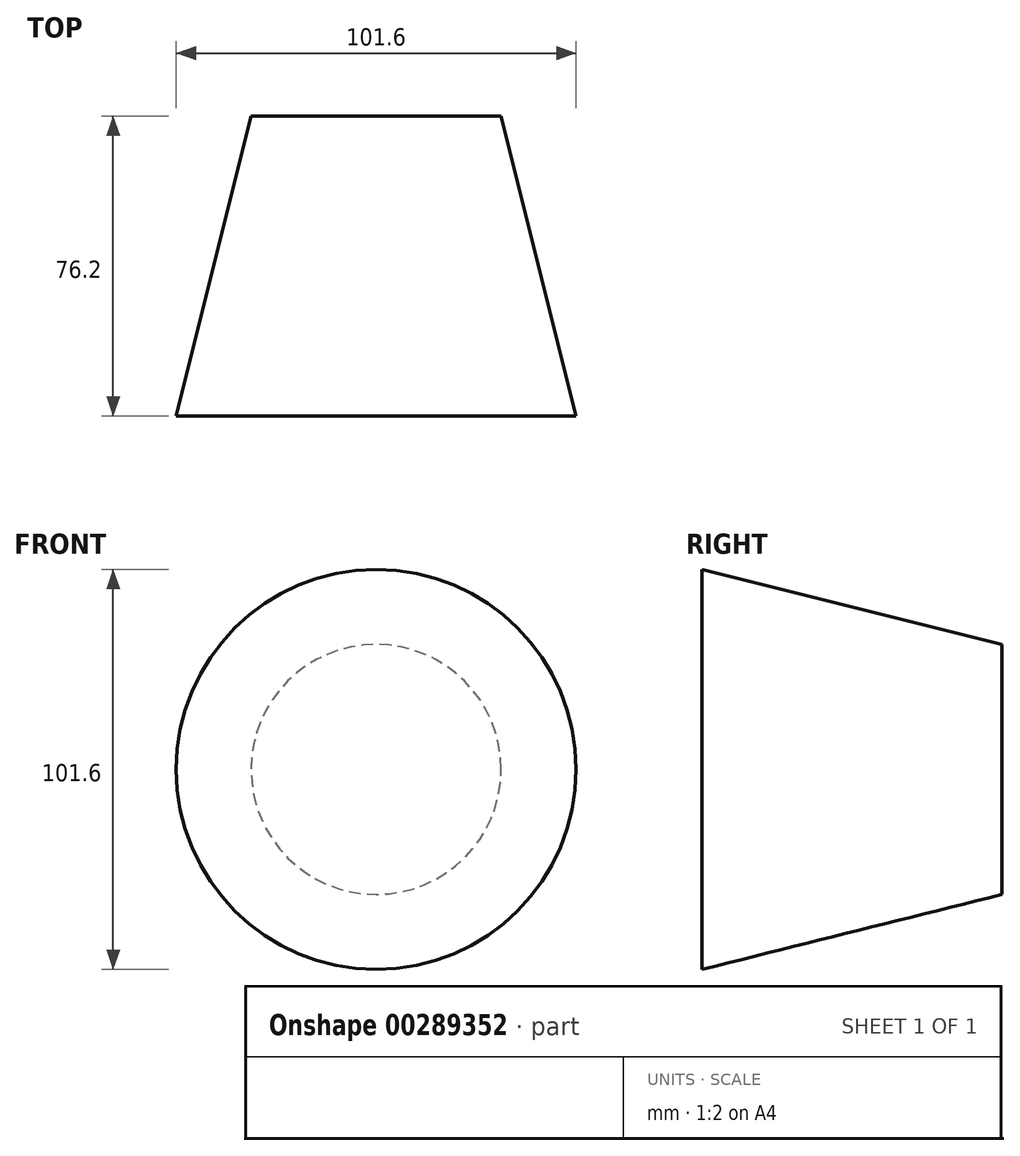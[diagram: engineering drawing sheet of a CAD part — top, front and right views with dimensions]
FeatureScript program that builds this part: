
annotation { "Feature Type Name" : "Feature", "Feature Type Description" : "" }
export const myFeature = defineFeature(function(context is Context, id is Id, definition is map)
    precondition{}
    {
        {
            var Q0;
            Q0=qCreatedBy(makeId("Front.planeOp"),FACE);
            var sketch = newSketch(context, id + "F0", { "sketchPlane" : qUnion([Q0])});
            skCircle(sketch, "E0", {"center": v(0, 0) * mm, "radius": 50.8 * mm});
            skSolve(sketch);
        }
        {
            var Q0;
            Q0=qCreatedBy(makeId("Front.planeOp"),FACE);
            cPlane(context, id + "F1", {"entities" : qUnion([Q0]), "cplaneType" : CPlaneType.OFFSET, "offset" : 76.2 * mm, "oppositeDirection" : true, "width" : 152.4 * mm, "height" : 152.4 * mm});
        }
        {
            var Q0;
            Q0=qCreatedBy(id+"F1.planeOp",FACE);
            var sketch = newSketch(context, id + "F2", { "sketchPlane" : qUnion([Q0])});
            skCircle(sketch, "E1", {"center": v(0, 0) * mm, "radius": 31.75 * mm});
            skSolve(sketch);
        }
        {
            var Q0;
            Q0 = qSketchRegion(id + "F0", true);
            var Q1;
            Q1 = qSketchRegion(id + "F2", true);
            loft(context, id + "F3", {"sheetProfilesArray" : [{ "sheetProfileEntities" : qUnion([Q0]) }, { "sheetProfileEntities" : qUnion([Q1]) }]});
        }
    });
